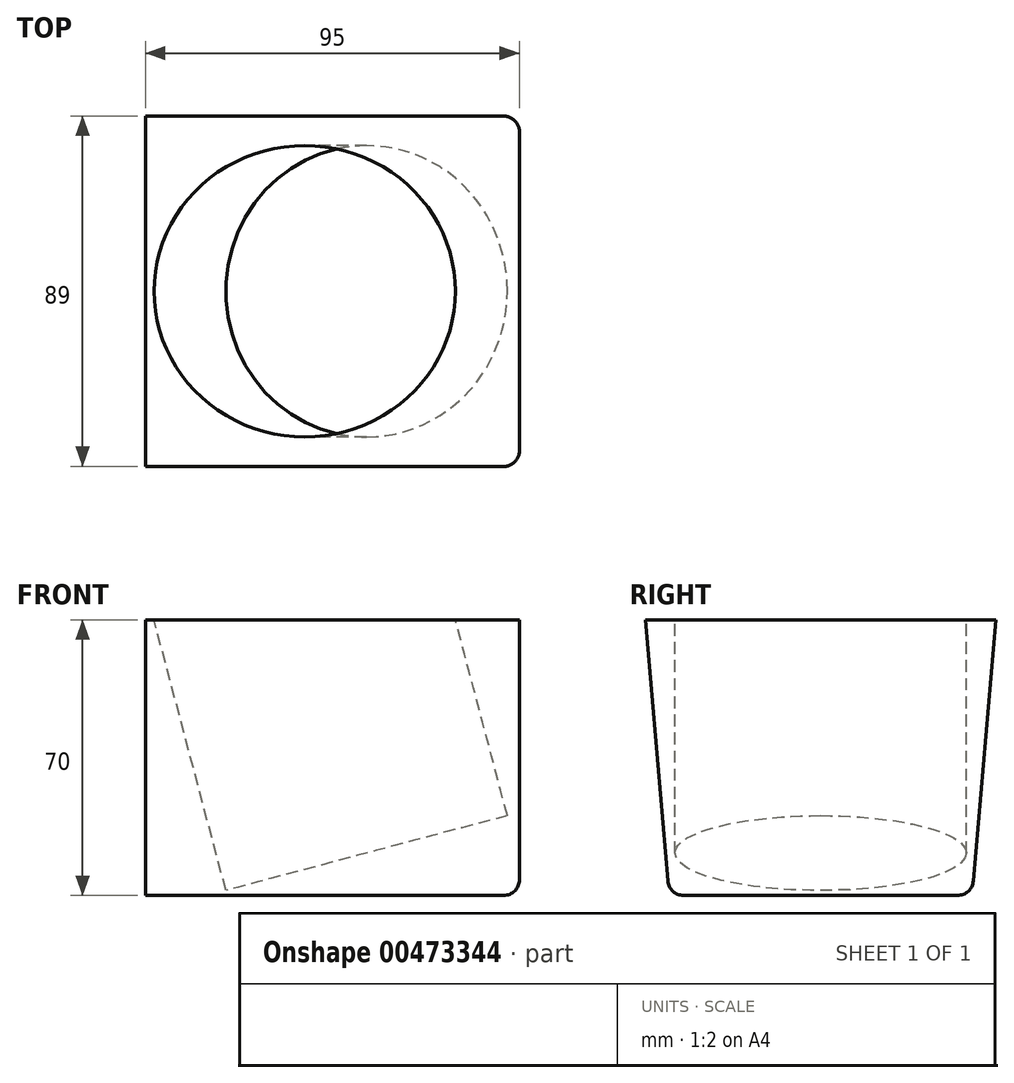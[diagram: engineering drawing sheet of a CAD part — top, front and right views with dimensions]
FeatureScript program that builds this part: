
annotation { "Feature Type Name" : "Feature", "Feature Type Description" : "" }
export const myFeature = defineFeature(function(context is Context, id is Id, definition is map)
    precondition{}
    {
        {
            var Q0;
            Q0=qCreatedBy(makeId("Top.planeOp"),FACE);
            var sketch = newSketch(context, id + "F0", { "sketchPlane" : qUnion([Q0])});
            skLineSegment(sketch, "E0.bottom", {"start": v(0, 0) * mm, "end": v(-95, 0) * mm});
            skLineSegment(sketch, "E0.top", {"start": v(0, -77) * mm, "end": v(-95, -77) * mm});
            skLineSegment(sketch, "E0.left", {"start": v(0, 0) * mm, "end": v(0, -77) * mm});
            skLineSegment(sketch, "E0.right", {"start": v(-95, 0) * mm, "end": v(-95, -77) * mm});
            skSolve(sketch);
        }
        {
            var Q0;
            Q0=qCreatedBy(makeId("Top.planeOp"),FACE);
            cPlane(context, id + "F1", {"entities" : qUnion([Q0]), "cplaneType" : CPlaneType.OFFSET, "offset" : 70 * mm, "width" : 150 * mm, "height" : 150 * mm});
        }
        {
            var Q0;
            Q0=qCreatedBy(id+"F1.planeOp",FACE);
            var sketch = newSketch(context, id + "F2", { "sketchPlane" : qUnion([Q0])});
            skLineSegment(sketch, "E1.bottom", {"start": v(0, 6) * mm, "end": v(-95, 6) * mm});
            skLineSegment(sketch, "E1.top", {"start": v(0, -83) * mm, "end": v(-95, -83) * mm});
            skLineSegment(sketch, "E1.left", {"start": v(0, 6) * mm, "end": v(0, -83) * mm});
            skLineSegment(sketch, "E1.right", {"start": v(-95, 6) * mm, "end": v(-95, -83) * mm});
            skSolve(sketch);
        }
        {
            var Q0;
            Q0=makeQuery(id+"F2.imprint","IMPRINT",FACE,{"disambiguationData":[TD([[makeQuery(id+"F2.imprint","IMPRINT",EDGE,{"derivedFrom":sQuery(id+"F2.wireOp",EDGE,"E1.bottom")}),1.0]])]});
            var Q1;
            Q1=makeQuery(id+"F0.imprint","IMPRINT",FACE,{"disambiguationData":[TD([[makeQuery(id+"F0.imprint","IMPRINT",EDGE,{"derivedFrom":sQuery(id+"F0.wireOp",EDGE,"E0.bottom")}),1.0]])]});
            loft(context, id + "F3", {"sheetProfilesArray" : [{ "sheetProfileEntities" : qUnion([Q0]) }, { "sheetProfileEntities" : qUnion([Q1]) }]});
        }
        {
            var Q0;
            Q0=makeQuery(id+"F3.opLoft","SWEPT_FACE",FACE,{"disambiguationData":[OSD([sQuery(id+"F0.wireOp",EDGE,"E0.top"),sQuery(id+"F0.wireOp",EDGE,"E0.left"),sQuery(id+"F0.wireOp",EDGE,"E0.right"),sQuery(id+"F2.wireOp",EDGE,"E1.top"),sQuery(id+"F2.wireOp",EDGE,"E1.left"),sQuery(id+"F2.wireOp",EDGE,"E1.right")])]});
            var sketch = newSketch(context, id + "F4", { "sketchPlane" : qUnion([Q0])});
            skLineSegment(sketch, "E2", {"start": v(0, 76.83) * mm, "end": v(0, 116.83) * mm, "construction": true});
            skLineSegment(sketch, "E3", {"start": v(-150, 76.83) * mm, "end": v(0, 116.83) * mm, "construction": true});
            skLineSegment(sketch, "E4", {"start": v(-95, 76.83) * mm, "end": v(-150, 76.83) * mm, "construction": true});
            skSolve(sketch);
        }
        {
            var Q0;
            Q0=makeQuery(id+"F3.opLoft","SWEPT_FACE",FACE,{"disambiguationData":[OSD([sQuery(id+"F0.wireOp",EDGE,"E0.bottom"),sQuery(id+"F0.wireOp",EDGE,"E0.left"),sQuery(id+"F0.wireOp",EDGE,"E0.right"),sQuery(id+"F2.wireOp",EDGE,"E1.bottom"),sQuery(id+"F2.wireOp",EDGE,"E1.left"),sQuery(id+"F2.wireOp",EDGE,"E1.right")])]});
            var sketch = newSketch(context, id + "F5", { "sketchPlane" : qUnion([Q0])});
            skLineSegment(sketch, "E5", {"start": v(0, 70.26) * mm, "end": v(0, 110.26) * mm, "construction": true});
            skLineSegment(sketch, "E6", {"start": v(95, 70.26) * mm, "end": v(150, 70.26) * mm, "construction": true});
            skLineSegment(sketch, "E7", {"start": v(0, 110.26) * mm, "end": v(150, 70.26) * mm, "construction": true});
            skSolve(sketch);
        }
        {
            var Q0;
            Q0=sQuery(id+"F5.wireOp",EDGE,"E7");
            var Q1;
            Q1=sQuery(id+"F4.wireOp",EDGE,"E3");
            cPlane(context, id + "F6", {"entities" : qUnion([Q0, Q1]), "cplaneType" : CPlaneType.LINE_ANGLE, "offset" : 25 * mm, "angle" : 0 * degree, "width" : 150 * mm, "height" : 150 * mm});
        }
        {
            var Q0;
            Q0=qCreatedBy(id+"F6.planeOp",FACE);
            var sketch = newSketch(context, id + "F7", { "sketchPlane" : qUnion([Q0])});
            skLineSegment(sketch, "E8", {"start": v(-33.84, 6) * mm, "end": v(-33.84, -38.5) * mm, "construction": true});
            skCircle(sketch, "E9", {"center": v(-34.74, -38.5) * mm, "radius": 37 * mm});
            skSolve(sketch);
        }
        {
            var Q0;
            Q0=makeQuery(id+"F7.imprint","IMPRINT",FACE,{"disambiguationData":[TD([[makeQuery(id+"F7.imprint","IMPRINT",EDGE,{"derivedFrom":sQuery(id+"F7.wireOp",EDGE,"bZrQLYIh-ME3Y-LaXI-Nw5T-CPILgFTqgrcL")}),1.0]])]});
            var Q1;
            Q1=makeQuery(id+"F7.imprint","IMPRINT",FACE,{"disambiguationData":[TD([[makeQuery(id+"F7.imprint","IMPRINT",EDGE,{"derivedFrom":sQuery(id+"F7.wireOp",EDGE,"E9")}),1.0]])]});
            extrude(context, id + "F8", {"entities" : qUnion([Q0, Q1]), "operationType" : NewBodyOperationType.REMOVE, "oppositeDirection" : true, "depth" : 85.8 * mm});
        }
        {
            var Q0;
            Q0=makeQuery(id+"F3.opLoft","MID_CAP_EDGE",EDGE,{"disambiguationData":[OSD([sQuery(id+"F0.wireOp",EDGE,"E0.top"),sQuery(id+"F0.wireOp",EDGE,"E0.left"),sQuery(id+"F0.wireOp",EDGE,"E0.right")])],"capPos":1.0});
            var Q1;
            Q1=makeQuery(id+"F3.opLoft","MID_CAP_EDGE",EDGE,{"disambiguationData":[OSD([sQuery(id+"F0.wireOp",EDGE,"E0.bottom"),sQuery(id+"F0.wireOp",EDGE,"E0.top"),sQuery(id+"F0.wireOp",EDGE,"E0.left")])],"capPos":1.0});
            var Q2;
            Q2=makeQuery(id+"F3.opLoft","MID_CAP_EDGE",EDGE,{"disambiguationData":[OSD([sQuery(id+"F0.wireOp",EDGE,"E0.bottom"),sQuery(id+"F0.wireOp",EDGE,"E0.left"),sQuery(id+"F0.wireOp",EDGE,"E0.right")])],"capPos":1.0});
            var Q3;
            Q3=makeQuery(id+"F3.opLoft","SWEPT_EDGE",EDGE,{"disambiguationData":[OSD([sQuery(id+"F0.wireOp",EDGE,"E0.top"),sQuery(id+"F0.wireOp",EDGE,"E0.left"),sQuery(id+"F2.wireOp",EDGE,"E1.top"),sQuery(id+"F2.wireOp",EDGE,"E1.left")])]});
            var Q4;
            Q4=makeQuery(id+"F3.opLoft","SWEPT_EDGE",EDGE,{"disambiguationData":[OSD([sQuery(id+"F0.wireOp",EDGE,"E0.bottom"),sQuery(id+"F0.wireOp",EDGE,"E0.left"),sQuery(id+"F2.wireOp",EDGE,"E1.bottom"),sQuery(id+"F2.wireOp",EDGE,"E1.left")])]});
            fillet(context, id + "F9", {"entities" : qUnion([Q0, Q1, Q2, Q3, Q4]), "radius" : 4 * mm, "tangentPropagation" : true, "allowEdgeOverflow" : false});
        }
    });
